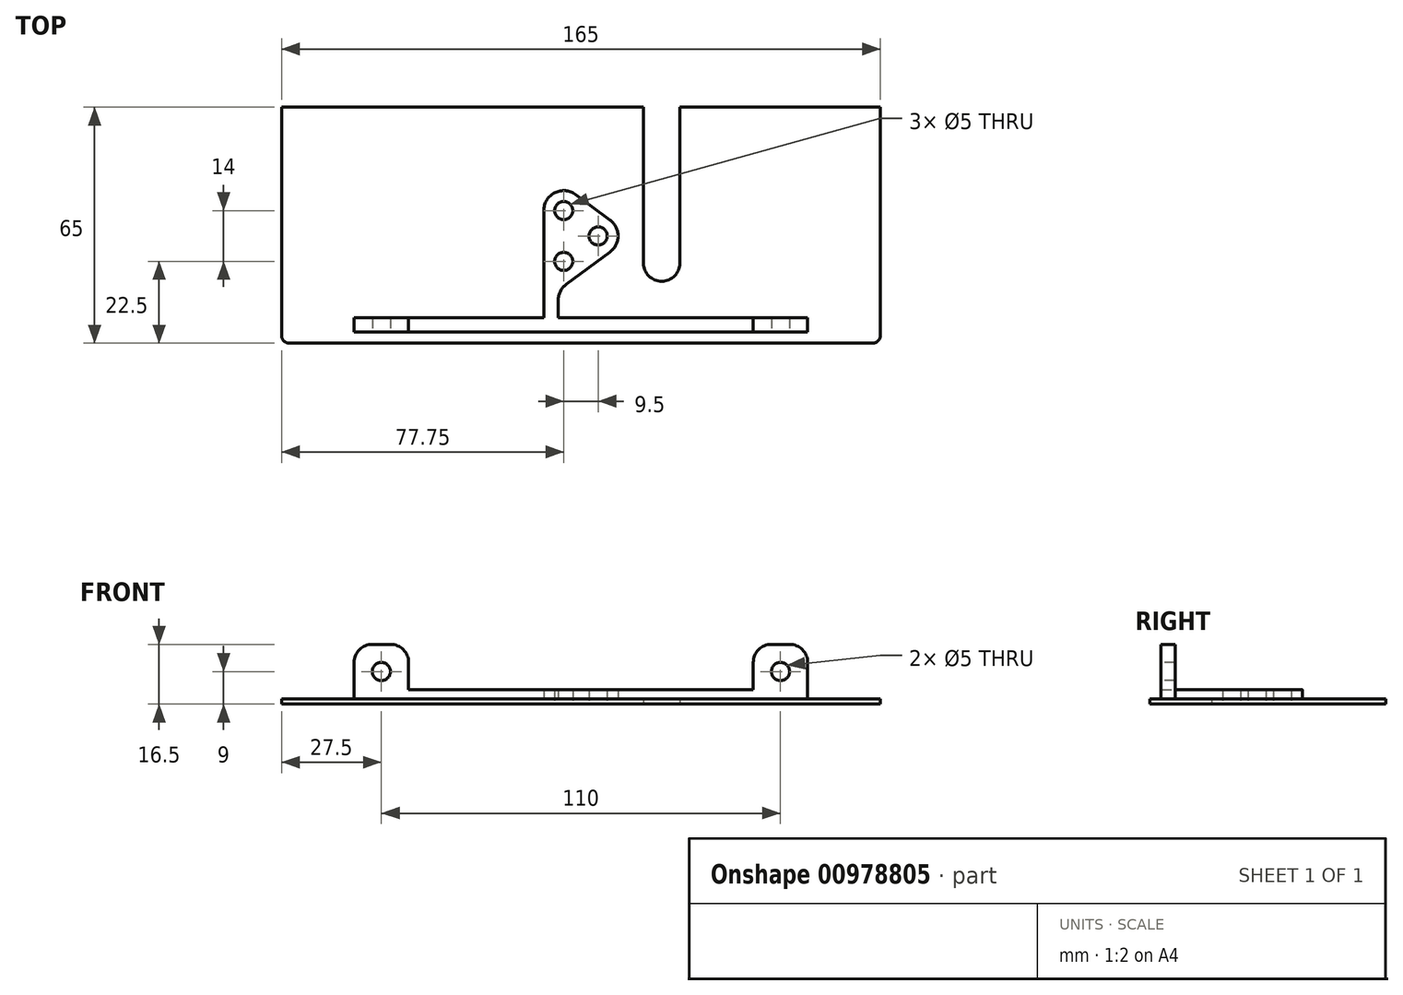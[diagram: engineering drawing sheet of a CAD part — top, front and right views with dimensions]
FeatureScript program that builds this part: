
annotation { "Feature Type Name" : "Feature", "Feature Type Description" : "" }
export const myFeature = defineFeature(function(context is Context, id is Id, definition is map)
    precondition{}
    {
        {
            assignVariable(context, id + "F0", {"name" : "wall", "anyValue" : 1.5});
        }
        {
            var Q0;
            Q0=qCreatedBy(makeId("Top.planeOp"),FACE);
            var sketch = newSketch(context, id + "F1", { "sketchPlane" : qUnion([Q0])});
            skLineSegment(sketch, "E0.bottom", {"start": v(-82.5, 0) * mm, "end": v(82.5, 0) * mm});
            skLineSegment(sketch, "E0.top", {"start": v(-80.5, 65) * mm, "end": v(80.5, 65) * mm});
            skLineSegment(sketch, "E0.left", {"start": v(-82.5, 0) * mm, "end": v(-82.5, 63) * mm});
            skLineSegment(sketch, "E0.right", {"start": v(82.5, 0) * mm, "end": v(82.5, 63) * mm});
            skPoint(sketch, "E1.visualSharp", {"position": v(-82.5, 65) * mm});
            skArc(sketch, "E1.filletArc", {"start": v(-80.5, 65) * mm, "mid": v(-81.91, 64.41) * mm, "end": v(-82.5, 63) * mm});
            skPoint(sketch, "E2.visualSharp", {"position": v(82.5, 65) * mm});
            skArc(sketch, "E2.filletArc", {"start": v(82.5, 63) * mm, "mid": v(81.91, 64.41) * mm, "end": v(80.5, 65) * mm});
            skArc(sketch, "E3", {"start": v(17.25, 43) * mm, "mid": v(22.25, 48) * mm, "end": v(27.25, 43) * mm});
            skLineSegment(sketch, "E4", {"start": v(17.25, 43) * mm, "end": v(17.25, 0) * mm});
            skLineSegment(sketch, "E5", {"start": v(27.25, 43) * mm, "end": v(27.25, 0) * mm});
            skLineSegment(sketch, "E6", {"start": v(0, 65) * mm, "end": v(0, 0) * mm, "construction": true});
            skCircle(sketch, "E7", {"center": v(4.75, 35.5) * mm, "radius": 2.5 * mm});
            skCircle(sketch, "E8", {"center": v(-4.75, 42.5) * mm, "radius": 2.5 * mm});
            skCircle(sketch, "E9", {"center": v(-4.75, 28.5) * mm, "radius": 2.5 * mm});
            skLineSegment(sketch, "E10", {"start": v(-4.75, 42.5) * mm, "end": v(-4.75, 28.5) * mm, "construction": true});
            skLineSegment(sketch, "E11", {"start": v(4.75, 35.5) * mm, "end": v(-4.75, 35.5) * mm, "construction": true});
            skPoint(sketch, "E11.endSnap0", {"position": v(-4.75, 35.5) * mm});
            skPoint(sketch, "E12", {"position": v(0, 35.5) * mm});
            skLineSegment(sketch, "E13", {"start": v(-4.75, 48) * mm, "end": v(-4.75, 23) * mm, "construction": true});
            skLineSegment(sketch, "E14", {"start": v(-4.75, 48) * mm, "end": v(22.25, 48) * mm, "construction": true});
            skLineSegment(sketch, "E15.bottom", {"start": v(-62.5, 62) * mm, "end": v(-47.5, 62) * mm});
            skLineSegment(sketch, "E15.top", {"start": v(-62.5, 58) * mm, "end": v(-47.5, 58) * mm});
            skLineSegment(sketch, "E15.left", {"start": v(-62.5, 62) * mm, "end": v(-62.5, 58) * mm});
            skLineSegment(sketch, "E15.right", {"start": v(-47.5, 62) * mm, "end": v(-47.5, 58) * mm});
            skLineSegment(sketch, "E16", {"start": v(-10.25, 28.5) * mm, "end": v(-10.25, 58) * mm});
            skLineSegment(sketch, "E17", {"start": v(8.01, 31.07) * mm, "end": v(-1.49, 24.07) * mm});
            skLineSegment(sketch, "E18", {"start": v(-7.25, 28.5) * mm, "end": v(-10.25, 28.5) * mm, "construction": true});
            skLineSegment(sketch, "E19", {"start": v(-3.27, 26.49) * mm, "end": v(-1.49, 24.07) * mm, "construction": true});
            skLineSegment(sketch, "E20", {"start": v(7.25, 35.5) * mm, "end": v(10.25, 35.5) * mm, "construction": true});
            skLineSegment(sketch, "E21", {"start": v(6.23, 33.49) * mm, "end": v(8.01, 31.07) * mm, "construction": true});
            skArc(sketch, "E22", {"start": v(-10.25, 28.5) * mm, "mid": v(-7.23, 23.6) * mm, "end": v(-1.49, 24.07) * mm});
            skArc(sketch, "E23", {"start": v(10.25, 35.5) * mm, "mid": v(9.66, 33.02) * mm, "end": v(8.01, 31.07) * mm});
            skArc(sketch, "E24.MirrorCS", {"start": v(10.25, 35.5) * mm, "mid": v(9.66, 37.98) * mm, "end": v(8.01, 39.93) * mm});
            skLineSegment(sketch, "E25", {"start": v(-6.25, 58) * mm, "end": v(-6.25, 53.22) * mm});
            skLineSegment(sketch, "E26", {"start": v(8.01, 39.93) * mm, "end": v(-4.01, 48.79) * mm});
            skArc(sketch, "E27.filletArc", {"start": v(-6.25, 53.22) * mm, "mid": v(-5.66, 50.74) * mm, "end": v(-4.01, 48.79) * mm});
            skPoint(sketch, "E28.visualSharp", {"position": v(-62.5, 62) * mm});
            skPoint(sketch, "E29.visualSharp", {"position": v(-62.5, 58) * mm});
            skPoint(sketch, "E30.visualSharp", {"position": v(-47.5, 62) * mm});
            skPoint(sketch, "E31.visualSharp", {"position": v(-47.5, 58) * mm});
            skLineSegment(sketch, "E32.MirrorCS", {"start": v(47.5, 62) * mm, "end": v(47.5, 58) * mm});
            skLineSegment(sketch, "E33.MirrorCS", {"start": v(62.5, 62) * mm, "end": v(62.5, 58) * mm});
            skPoint(sketch, "E34.MirrorP", {"position": v(62.5, 62) * mm});
            skLineSegment(sketch, "E35.MirrorCS", {"start": v(62.5, 58) * mm, "end": v(47.5, 58) * mm});
            skLineSegment(sketch, "E36.MirrorCS", {"start": v(62.5, 62) * mm, "end": v(47.5, 62) * mm});
            skPoint(sketch, "E37.MirrorP", {"position": v(47.5, 58) * mm});
            skPoint(sketch, "E38.MirrorP", {"position": v(62.5, 58) * mm});
            skPoint(sketch, "E39.MirrorP", {"position": v(47.5, 62) * mm});
            skLineSegment(sketch, "E40", {"start": v(-47.5, 58) * mm, "end": v(47.5, 58) * mm});
            skLineSegment(sketch, "E41", {"start": v(-47.5, 62) * mm, "end": v(47.5, 62) * mm});
            skSolve(sketch);
        }
        {
            var Q0;
            Q0=makeQuery(id+"F1.imprint","IMPRINT",FACE,{"disambiguationData":[TD([[makeQuery(id+"F1.imprint","IMPRINT",EDGE,{"derivedFrom":sQuery(id+"F1.wireOp",EDGE,"E0.top")}),-1.0]])]});
            extrude(context, id + "F2", {"entities" : qUnion([Q0]), "depth" : (getVariable(context, 'wall')) * mm, "offsetDistance" : 25 * mm});
        }
        {
            var Q0;
            Q0=makeQuery(id+"F1.imprint","IMPRINT",FACE,{"disambiguationData":[TD([[makeQuery(id+"F1.imprint","IMPRINT",EDGE,{"derivedFrom":sQuery(id+"F1.wireOp",EDGE,"E15.bottom")}),-1.0]])]});
            var Q1;
            Q1=makeQuery(id+"F1.imprint","IMPRINT",FACE,{"disambiguationData":[TD([[makeQuery(id+"F1.imprint","IMPRINT",EDGE,{"derivedFrom":sQuery(id+"F1.wireOp",EDGE,"E32.MirrorCS")}),1.0]])]});
            extrude(context, id + "F3", {"entities" : qUnion([Q0, Q1]), "operationType" : NewBodyOperationType.ADD, "depth" : (getVariable(context, 'wall') + 15) * mm, "offsetDistance" : 25 * mm});
        }
        {
            var Q0;
            Q0=makeQuery(id+"F1.imprint","IMPRINT",FACE,{"disambiguationData":[TD([[makeQuery(id+"F1.imprint","IMPRINT",EDGE,{"derivedFrom":sQuery(id+"F1.wireOp",EDGE,"E15.right")}),1.0]])]});
            var Q1;
            Q1=makeQuery(id+"F1.imprint","IMPRINT",FACE,{"disambiguationData":[TD([[makeQuery(id+"F1.imprint","IMPRINT",EDGE,{"derivedFrom":sQuery(id+"F1.wireOp",EDGE,"E7")}),-1.0]])]});
            extrude(context, id + "F4", {"entities" : qUnion([Q0, Q1]), "operationType" : NewBodyOperationType.ADD, "depth" : 4 * mm, "offsetDistance" : 25 * mm});
        }
        {
            var Q0;
            Q0=makeQuery(id+"F4.boolean.opBoolean","MERGE",FACE,{"derivedFrom":[makeQuery(id+"F3.opExtrude","SWEPT_FACE",FACE,{"disambiguationData":[OSD([sQuery(id+"F1.wireOp",EDGE,"E15.bottom")])]}),makeQuery(id+"F3.opExtrude","SWEPT_FACE",FACE,{"disambiguationData":[OSD([sQuery(id+"F1.wireOp",EDGE,"E36.MirrorCS")])]}),makeQuery(id+"F4.opExtrude","SWEPT_FACE",FACE,{"disambiguationData":[OSD([sQuery(id+"F1.wireOp",EDGE,"E41")])]})]});
            var sketch = newSketch(context, id + "F5", { "sketchPlane" : qUnion([Q0])});
            skLineSegment(sketch, "E42", {"start": v(55, 16.5) * mm, "end": v(55, 1.5) * mm, "construction": true});
            skCircle(sketch, "E43", {"center": v(55, 9) * mm, "radius": 2.5 * mm});
            skLineSegment(sketch, "E44", {"start": v(-55, 16.5) * mm, "end": v(-55, 1.5) * mm, "construction": true});
            skCircle(sketch, "E45", {"center": v(-55, 9) * mm, "radius": 2.5 * mm});
            skSolve(sketch);
        }
        {
            var Q0;
            Q0=makeQuery(id+"F5.imprint","IMPRINT",FACE,{"disambiguationData":[TD([[makeQuery(id+"F5.imprint","IMPRINT",EDGE,{"derivedFrom":sQuery(id+"F5.wireOp",EDGE,"E43")}),1.0]])]});
            var Q1;
            Q1=makeQuery(id+"F5.imprint","IMPRINT",FACE,{"disambiguationData":[TD([[makeQuery(id+"F5.imprint","IMPRINT",EDGE,{"derivedFrom":sQuery(id+"F5.wireOp",EDGE,"E45")}),1.0]])]});
            extrude(context, id + "F6", {"entities" : qUnion([Q0, Q1]), "operationType" : NewBodyOperationType.REMOVE, "endBound" : BoundingType.THROUGH_ALL, "oppositeDirection" : true, "depth" : 25 * mm, "offsetDistance" : 25 * mm});
        }
        {
            var Q0;
            Q0=makeQuery(id+"F3.opExtrude","CAP_EDGE",EDGE,{"disambiguationData":[OSD([sQuery(id+"F1.wireOp",EDGE,"E15.left")])],"isStart":false});
            var Q1;
            Q1=makeQuery(id+"F3.opExtrude","CAP_EDGE",EDGE,{"disambiguationData":[OSD([sQuery(id+"F1.wireOp",EDGE,"E15.right")])],"isStart":false});
            var Q2;
            Q2=makeQuery(id+"F3.opExtrude","CAP_EDGE",EDGE,{"disambiguationData":[OSD([sQuery(id+"F1.wireOp",EDGE,"E32.MirrorCS")])],"isStart":false});
            var Q3;
            Q3=makeQuery(id+"F3.opExtrude","CAP_EDGE",EDGE,{"disambiguationData":[OSD([sQuery(id+"F1.wireOp",EDGE,"E33.MirrorCS")])],"isStart":false});
            fillet(context, id + "F7", {"entities" : qUnion([Q0, Q1, Q2, Q3]), "radius" : 5 * mm, "tangentPropagation" : true, "allowEdgeOverflow" : false});
        }
        {
            var Q0;
            Q0=makeQuery(id+"F2.opExtrude","SWEPT_BODY",BODY,{"disambiguationData":[OSD([sQuery(id+"F1.wireOp",EDGE,"E0.bottom"),sQuery(id+"F1.wireOp",EDGE,"E0.top"),sQuery(id+"F1.wireOp",EDGE,"E0.left"),sQuery(id+"F1.wireOp",EDGE,"E0.right"),sQuery(id+"F1.wireOp",EDGE,"E1.filletArc"),sQuery(id+"F1.wireOp",EDGE,"E2.filletArc"),sQuery(id+"F1.wireOp",EDGE,"E3"),sQuery(id+"F1.wireOp",EDGE,"E4"),sQuery(id+"F1.wireOp",EDGE,"E5"),sQuery(id+"F1.wireOp",EDGE,"E15.bottom"),sQuery(id+"F1.wireOp",EDGE,"E15.top"),sQuery(id+"F1.wireOp",EDGE,"E15.left"),sQuery(id+"F1.wireOp",EDGE,"E16"),sQuery(id+"F1.wireOp",EDGE,"E17"),sQuery(id+"F1.wireOp",EDGE,"E22"),sQuery(id+"F1.wireOp",EDGE,"E23"),sQuery(id+"F1.wireOp",EDGE,"E24.MirrorCS"),sQuery(id+"F1.wireOp",EDGE,"E25"),sQuery(id+"F1.wireOp",EDGE,"E26"),sQuery(id+"F1.wireOp",EDGE,"E27.filletArc"),sQuery(id+"F1.wireOp",EDGE,"E28.filletArc"),sQuery(id+"F1.wireOp",EDGE,"E29.filletArc"),sQuery(id+"F1.wireOp",EDGE,"E33.MirrorCS"),sQuery(id+"F1.wireOp",EDGE,"3ecd585d-c63c-40e6-b4da-5e53aae952a92.MirrorCS"),sQuery(id+"F1.wireOp",EDGE,"3ecd585d-c63c-40e6-b4da-5e53aae952a95.MirrorCS"),sQuery(id+"F1.wireOp",EDGE,"E35.MirrorCS"),sQuery(id+"F1.wireOp",EDGE,"E36.MirrorCS"),sQuery(id+"F1.wireOp",EDGE,"E40"),sQuery(id+"F1.wireOp",EDGE,"E41")])]});
            var Q1;
            Q1=qCreatedBy(makeId("Top.planeOp"),FACE);
            mirror(context, id + "F8", {"entities" : qUnion([Q0]), "mirrorPlane" : qUnion([Q1])});
        }
        {
            var Q0;
            Q0=makeQuery(id+"F2.opExtrude","SWEPT_BODY",BODY,{"disambiguationData":[OSD([sQuery(id+"F1.wireOp",EDGE,"E0.bottom"),sQuery(id+"F1.wireOp",EDGE,"E0.top"),sQuery(id+"F1.wireOp",EDGE,"E0.left"),sQuery(id+"F1.wireOp",EDGE,"E0.right"),sQuery(id+"F1.wireOp",EDGE,"E1.filletArc"),sQuery(id+"F1.wireOp",EDGE,"E2.filletArc"),sQuery(id+"F1.wireOp",EDGE,"E3"),sQuery(id+"F1.wireOp",EDGE,"E4"),sQuery(id+"F1.wireOp",EDGE,"E5"),sQuery(id+"F1.wireOp",EDGE,"E15.bottom"),sQuery(id+"F1.wireOp",EDGE,"E15.top"),sQuery(id+"F1.wireOp",EDGE,"E15.left"),sQuery(id+"F1.wireOp",EDGE,"E16"),sQuery(id+"F1.wireOp",EDGE,"E17"),sQuery(id+"F1.wireOp",EDGE,"E22"),sQuery(id+"F1.wireOp",EDGE,"E23"),sQuery(id+"F1.wireOp",EDGE,"E24.MirrorCS"),sQuery(id+"F1.wireOp",EDGE,"E25"),sQuery(id+"F1.wireOp",EDGE,"E26"),sQuery(id+"F1.wireOp",EDGE,"E27.filletArc"),sQuery(id+"F1.wireOp",EDGE,"E28.filletArc"),sQuery(id+"F1.wireOp",EDGE,"E29.filletArc"),sQuery(id+"F1.wireOp",EDGE,"E33.MirrorCS"),sQuery(id+"F1.wireOp",EDGE,"3ecd585d-c63c-40e6-b4da-5e53aae952a92.MirrorCS"),sQuery(id+"F1.wireOp",EDGE,"3ecd585d-c63c-40e6-b4da-5e53aae952a95.MirrorCS"),sQuery(id+"F1.wireOp",EDGE,"E35.MirrorCS"),sQuery(id+"F1.wireOp",EDGE,"E36.MirrorCS"),sQuery(id+"F1.wireOp",EDGE,"E40"),sQuery(id+"F1.wireOp",EDGE,"E41")])]});
            deleteBodies(context, id + "F9", {"entities" : qUnion([Q0])});
        }
        {
            var Q0;
            Q0=makeQuery(id+"F8.opPattern","COPY",BODY,{"derivedFrom":makeQuery(id+"F2.opExtrude","SWEPT_BODY",BODY,{"disambiguationData":[OSD([sQuery(id+"F1.wireOp",EDGE,"E0.bottom"),sQuery(id+"F1.wireOp",EDGE,"E0.top"),sQuery(id+"F1.wireOp",EDGE,"E0.left"),sQuery(id+"F1.wireOp",EDGE,"E0.right"),sQuery(id+"F1.wireOp",EDGE,"E1.filletArc"),sQuery(id+"F1.wireOp",EDGE,"E2.filletArc"),sQuery(id+"F1.wireOp",EDGE,"E3"),sQuery(id+"F1.wireOp",EDGE,"E4"),sQuery(id+"F1.wireOp",EDGE,"E5"),sQuery(id+"F1.wireOp",EDGE,"E15.bottom"),sQuery(id+"F1.wireOp",EDGE,"E15.top"),sQuery(id+"F1.wireOp",EDGE,"E15.left"),sQuery(id+"F1.wireOp",EDGE,"E16"),sQuery(id+"F1.wireOp",EDGE,"E17"),sQuery(id+"F1.wireOp",EDGE,"E22"),sQuery(id+"F1.wireOp",EDGE,"E23"),sQuery(id+"F1.wireOp",EDGE,"E24.MirrorCS"),sQuery(id+"F1.wireOp",EDGE,"E25"),sQuery(id+"F1.wireOp",EDGE,"E26"),sQuery(id+"F1.wireOp",EDGE,"E27.filletArc"),sQuery(id+"F1.wireOp",EDGE,"E33.MirrorCS"),sQuery(id+"F1.wireOp",EDGE,"E35.MirrorCS"),sQuery(id+"F1.wireOp",EDGE,"E36.MirrorCS"),sQuery(id+"F1.wireOp",EDGE,"E40"),sQuery(id+"F1.wireOp",EDGE,"E41")])]}),"instanceName":"1"});
            var Q1;
            {var subQ0=sQuery(id+"F1.wireOp",EDGE,"E0.bottom");Q1=makeQuery(id+"F8.opPattern","COPY",EDGE,{"derivedFrom":makeQuery(id+"F2.opExtrude","CAP_EDGE",EDGE,{"disambiguationData":[OSD([subQ0]),TDD([makeQuery(id+"F1.imprint","IMPRINT",EDGE,{"disambiguationData":[TD([[makeQuery(id+"F1.imprint","INTERSECT",VERTEX,{"derivedFrom":[subQ0,sQuery(id+"F1.wireOp",EDGE,"E0.left")]}),-1.0]])],"derivedFrom":subQ0})])],"isStart":true}),"instanceName":"1"});}
            transform(context, id + "F10", {"entities" : qUnion([Q0]), "transformType" : TransformType.ROTATION, "transformAxis" : qUnion([Q1]), "angle" : 180 * degree, "makeCopy" : false});
        }
    });
